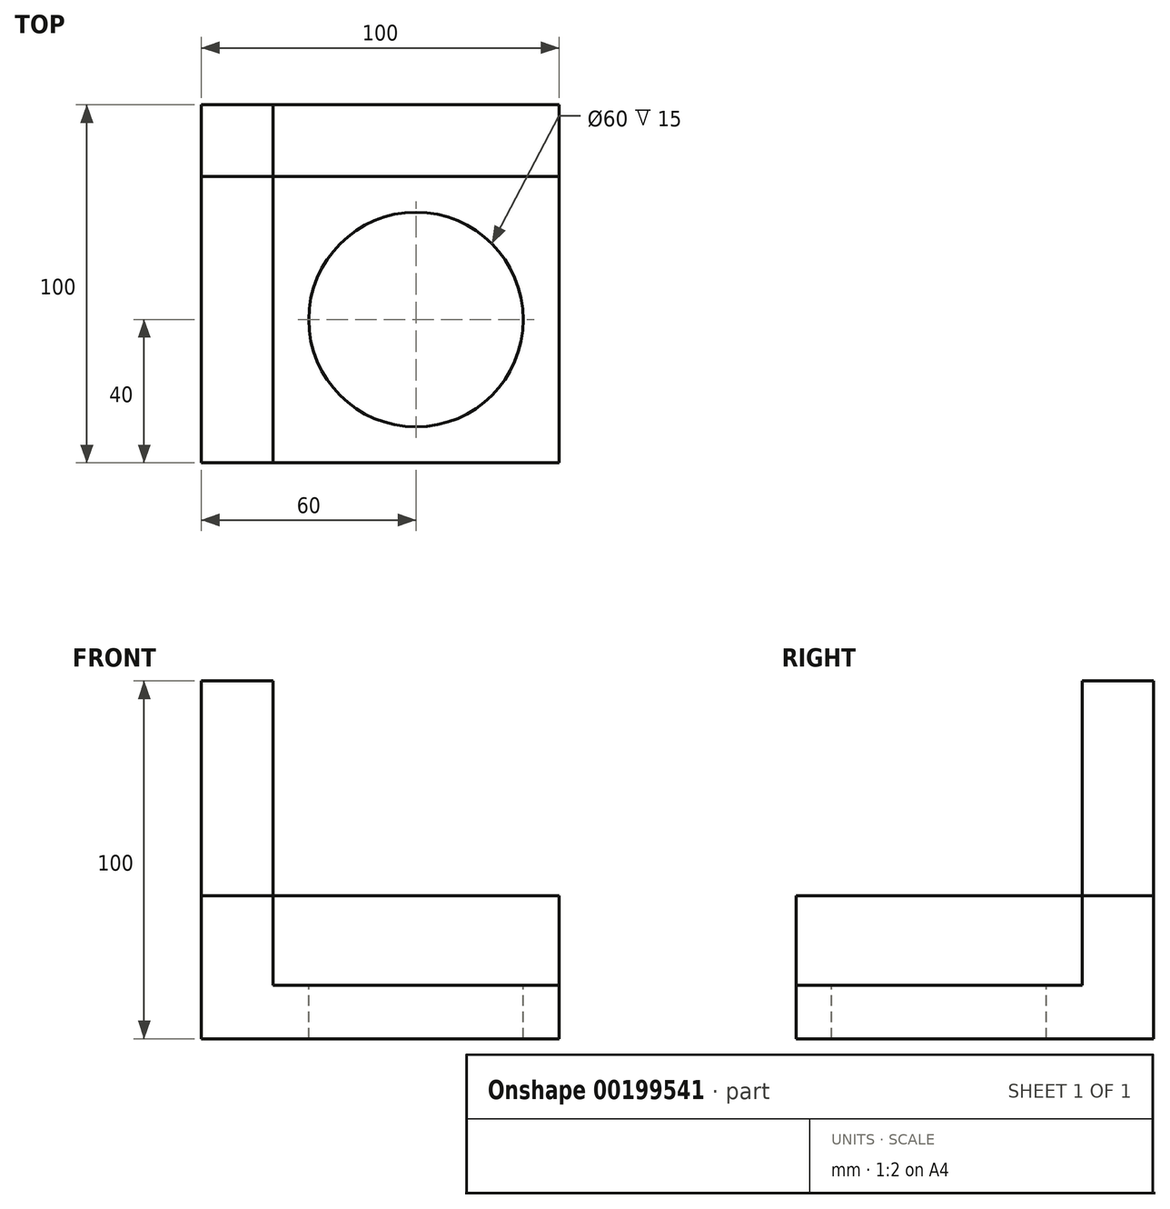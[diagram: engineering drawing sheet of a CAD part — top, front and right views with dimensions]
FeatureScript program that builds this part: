
annotation { "Feature Type Name" : "Feature", "Feature Type Description" : "" }
export const myFeature = defineFeature(function(context is Context, id is Id, definition is map)
    precondition{}
    {
        {
            var Q0;
            Q0=qCreatedBy(makeId("Top.planeOp"),FACE);
            var sketch = newSketch(context, id + "F0", { "sketchPlane" : qUnion([Q0])});
            skLineSegment(sketch, "E0.bottom", {"start": v(50, 50) * mm, "end": v(-50, 50) * mm});
            skLineSegment(sketch, "E0.top", {"start": v(50, -50) * mm, "end": v(-50, -50) * mm});
            skLineSegment(sketch, "E0.left", {"start": v(50, 50) * mm, "end": v(50, -50) * mm});
            skLineSegment(sketch, "E0.right", {"start": v(-50, 50) * mm, "end": v(-50, -50) * mm});
            skPoint(sketch, "E0.middle", {"position": v(0, 0) * mm});
            skSolve(sketch);
        }
        {
            var Q0;
            Q0 = qSketchRegion(id + "F0", true);
            extrude(context, id + "F1", {"entities" : qUnion([Q0]), "depth" : 15 * mm});
        }
        {
            var Q0;
            Q0=makeQuery(id+"F1.opExtrude","CAP_FACE",FACE,{"disambiguationData":[OSD([sQuery(id+"F0.wireOp",EDGE,"E0.bottom"),sQuery(id+"F0.wireOp",EDGE,"E0.top"),sQuery(id+"F0.wireOp",EDGE,"E0.left"),sQuery(id+"F0.wireOp",EDGE,"E0.right")])],"isStart":false});
            var sketch = newSketch(context, id + "F2", { "sketchPlane" : qUnion([Q0])});
            skLineSegment(sketch, "E1", {"start": v(-50, 50) * mm, "end": v(-30, 50) * mm, "construction": true});
            skLineSegment(sketch, "E2", {"start": v(-30, 50) * mm, "end": v(-30, 30) * mm, "construction": true});
            skLineSegment(sketch, "E3", {"start": v(50, 30) * mm, "end": v(-30, 30) * mm});
            skLineSegment(sketch, "E4", {"start": v(-30, -50) * mm, "end": v(-30, 30) * mm});
            skLineSegment(sketch, "E5", {"start": v(50, 30) * mm, "end": v(50, 50) * mm});
            skLineSegment(sketch, "E6", {"start": v(50, 50) * mm, "end": v(-50, 50) * mm});
            skLineSegment(sketch, "E7", {"start": v(-50, -50) * mm, "end": v(-50, 50) * mm});
            skLineSegment(sketch, "E8", {"start": v(-50, -50) * mm, "end": v(-30, -50) * mm});
            skSolve(sketch);
        }
        {
            var Q0;
            Q0 = qSketchRegion(id + "F2", true);
            extrude(context, id + "F3", {"entities" : qUnion([Q0]), "operationType" : NewBodyOperationType.ADD, "depth" : 25 * mm});
        }
        {
            var Q0;
            Q0=makeQuery(id+"F1.opExtrude","CAP_FACE",FACE,{"disambiguationData":[OSD([sQuery(id+"F0.wireOp",EDGE,"E0.bottom"),sQuery(id+"F0.wireOp",EDGE,"E0.top"),sQuery(id+"F0.wireOp",EDGE,"E0.left"),sQuery(id+"F0.wireOp",EDGE,"E0.right")])],"isStart":false});
            var sketch = newSketch(context, id + "F4", { "sketchPlane" : qUnion([Q0])});
            skLineSegment(sketch, "E9", {"start": v(-30, -10) * mm, "end": v(50, -10) * mm, "construction": true});
            skLineSegment(sketch, "E10", {"start": v(10, 30) * mm, "end": v(10, -50) * mm, "construction": true});
            skCircle(sketch, "E11", {"center": v(10, -10) * mm, "radius": 30 * mm});
            skSolve(sketch);
        }
        {
            var Q0;
            Q0 = qSketchRegion(id + "F4", true);
            extrude(context, id + "F5", {"entities" : qUnion([Q0]), "operationType" : NewBodyOperationType.REMOVE, "endBound" : BoundingType.THROUGH_ALL, "oppositeDirection" : true, "depth" : 25 * mm});
        }
        {
            var Q0;
            Q0=makeQuery(id+"F3.opExtrude","CAP_FACE",FACE,{"disambiguationData":[OSD([sQuery(id+"F2.wireOp",EDGE,"E3"),sQuery(id+"F2.wireOp",EDGE,"E4"),sQuery(id+"F2.wireOp",EDGE,"E5"),sQuery(id+"F2.wireOp",EDGE,"E6"),sQuery(id+"F2.wireOp",EDGE,"E7"),sQuery(id+"F2.wireOp",EDGE,"E8")])],"isStart":false});
            var sketch = newSketch(context, id + "F6", { "sketchPlane" : qUnion([Q0])});
            skLineSegment(sketch, "E12.bottom", {"start": v(-50, 50) * mm, "end": v(-30, 50) * mm});
            skLineSegment(sketch, "E12.top", {"start": v(-50, 30) * mm, "end": v(-30, 30) * mm});
            skLineSegment(sketch, "E12.left", {"start": v(-50, 50) * mm, "end": v(-50, 30) * mm});
            skLineSegment(sketch, "E12.right", {"start": v(-30, 50) * mm, "end": v(-30, 30) * mm});
            skSolve(sketch);
        }
        {
            var Q0;
            Q0 = qSketchRegion(id + "F6", true);
            extrude(context, id + "F7", {"entities" : qUnion([Q0]), "operationType" : NewBodyOperationType.ADD, "depth" : 60 * mm});
        }
    });
